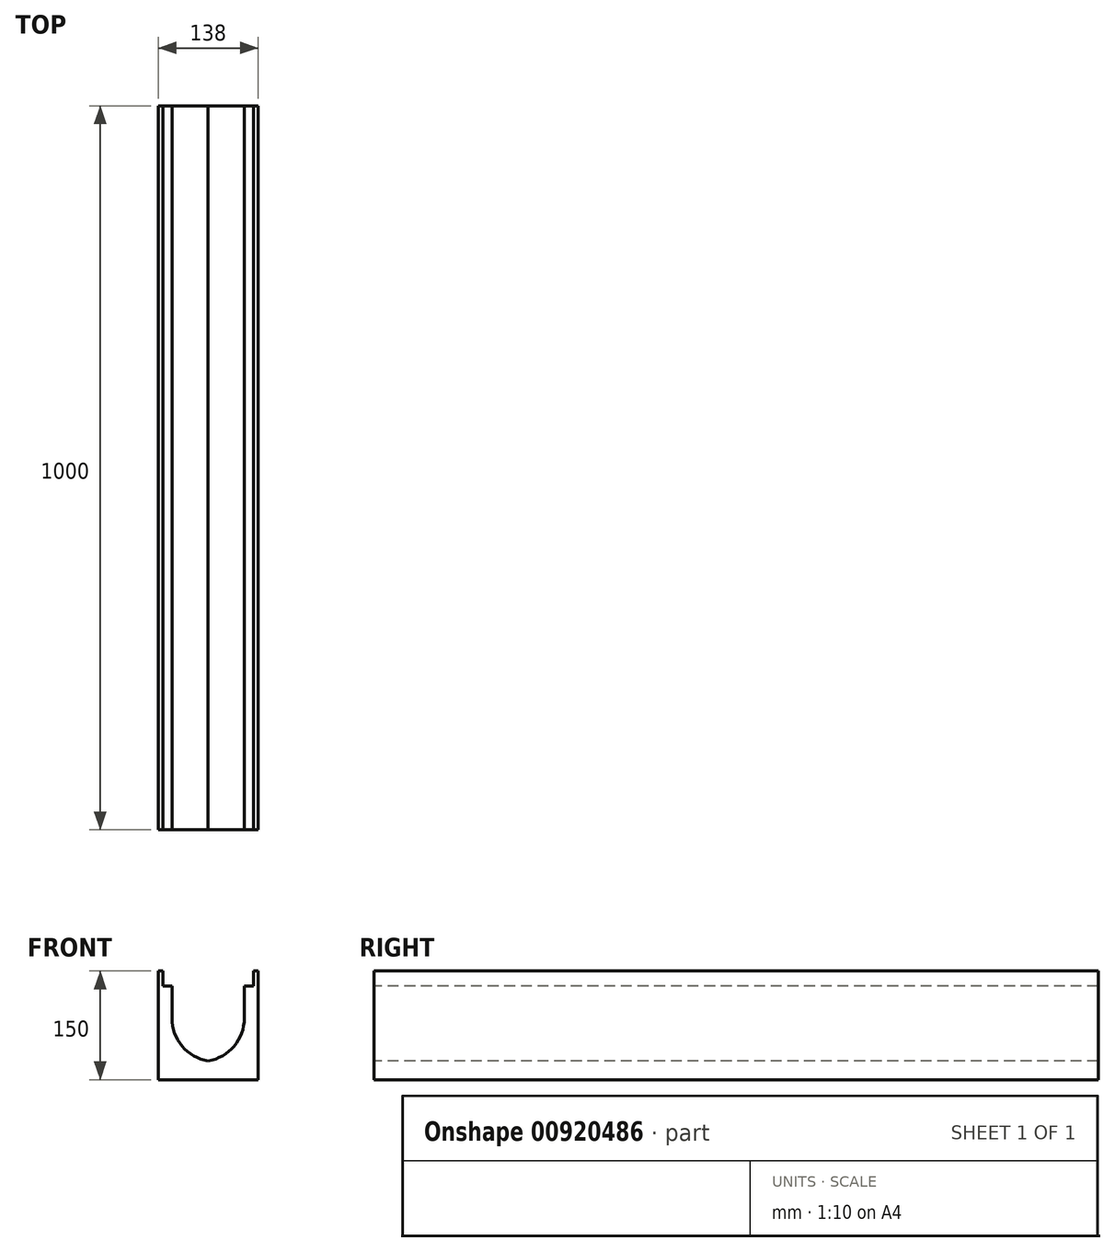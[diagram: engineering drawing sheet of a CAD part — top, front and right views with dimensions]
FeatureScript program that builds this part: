
annotation { "Feature Type Name" : "Feature", "Feature Type Description" : "" }
export const myFeature = defineFeature(function(context is Context, id is Id, definition is map)
    precondition{}
    {
        {
            var Q0;
            Q0=qCreatedBy(makeId("Front.planeOp"),FACE);
            var sketch = newSketch(context, id + "F0", { "sketchPlane" : qUnion([Q0])});
            skLineSegment(sketch, "E0.bottom", {"start": v(0, 0) * mm, "end": v(6.5, 0) * mm});
            skLineSegment(sketch, "E0.top", {"start": v(0, -150) * mm, "end": v(138, -150) * mm});
            skLineSegment(sketch, "E0.left", {"start": v(0, 0) * mm, "end": v(0, -150) * mm});
            skLineSegment(sketch, "E0.right", {"start": v(138, 0) * mm, "end": v(138, -150) * mm});
            skLineSegment(sketch, "E1", {"start": v(119, -21) * mm, "end": v(119, -65) * mm});
            skLineSegment(sketch, "E2", {"start": v(6.5, 0) * mm, "end": v(6.5, -21) * mm});
            skLineSegment(sketch, "E3", {"start": v(131.5, 0) * mm, "end": v(131.5, -21) * mm});
            skLineSegment(sketch, "E4", {"start": v(6.5, -21) * mm, "end": v(19, -21) * mm});
            skLineSegment(sketch, "E5.trimOffspring", {"start": v(19, -21) * mm, "end": v(19, -65) * mm});
            skPoint(sketch, "E6.start.orphan", {"position": v(19, 17.47) * mm});
            skLineSegment(sketch, "E7.trimOffspring", {"start": v(131.5, 0) * mm, "end": v(138, 0) * mm});
            skPoint(sketch, "E8.visualSharp", {"position": v(19, -125) * mm});
            skArc(sketch, "E8.filletArc", {"start": v(19, -65) * mm, "mid": v(33.17, -103.73) * mm, "end": v(69, -124.16) * mm});
            skPoint(sketch, "E9.visualSharp", {"position": v(119, -125) * mm});
            skArc(sketch, "E9.filletArc", {"start": v(69, -124.16) * mm, "mid": v(104.83, -103.73) * mm, "end": v(119, -65) * mm});
            skPoint(sketch, "E10.orphan", {"position": v(6.5, 17.47) * mm});
            skLineSegment(sketch, "E11.trimOffspring", {"start": v(119, -21) * mm, "end": v(131.5, -21) * mm});
            skSolve(sketch);
        }
        {
            var Q0;
            Q0=makeQuery(id+"F0.imprint","IMPRINT",FACE,{"disambiguationData":[TD([[makeQuery(id+"F0.imprint","IMPRINT",EDGE,{"derivedFrom":sQuery(id+"F0.wireOp",EDGE,"E0.bottom")}),-1.0]])]});
            extrude(context, id + "F1", {"entities" : qUnion([Q0]), "oppositeDirection" : true, "depth" : 1000 * mm, "offsetDistance" : 25 * mm});
        }
    });
